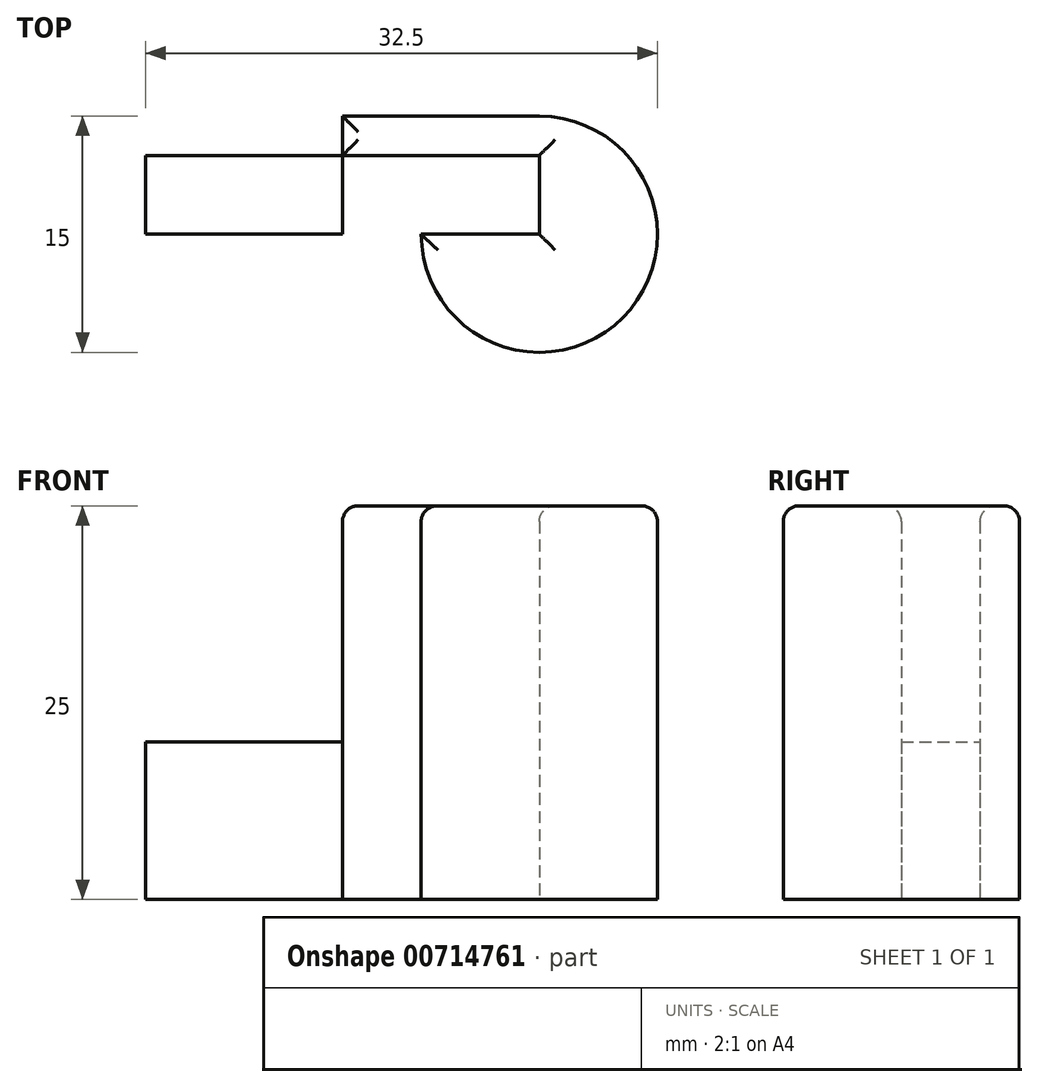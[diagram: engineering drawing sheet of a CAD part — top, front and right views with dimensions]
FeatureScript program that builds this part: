
annotation { "Feature Type Name" : "Feature", "Feature Type Description" : "" }
export const myFeature = defineFeature(function(context is Context, id is Id, definition is map)
    precondition{}
    {
        {
            var Q0;
            Q0=qCreatedBy(makeId("Top.planeOp"),FACE);
            var sketch = newSketch(context, id + "F0", { "sketchPlane" : qUnion([Q0])});
            skArc(sketch, "E0", {"start": v(-12.5, 5) * mm, "mid": v(-16.04, -3.54) * mm, "end": v(-7.5, 0) * mm});
            skArc(sketch, "E1", {"start": v(-7.5, 0) * mm, "mid": v(5.3, -5.3) * mm, "end": v(0, 7.5) * mm});
            skLineSegment(sketch, "E2", {"start": v(-12.5, 0) * mm, "end": v(0, 0) * mm, "construction": true});
            skLineSegment(sketch, "E3.bottom", {"start": v(-12.5, 0) * mm, "end": v(0, 0) * mm});
            skLineSegment(sketch, "E3.top", {"start": v(-12.5, 7.5) * mm, "end": v(0, 7.5) * mm});
            skLineSegment(sketch, "E3.left", {"start": v(-12.5, 0) * mm, "end": v(-12.5, 7.5) * mm});
            skLineSegment(sketch, "E3.right", {"start": v(0, 0) * mm, "end": v(0, 7.5) * mm});
            skArc(sketch, "E4.MirrorCS", {"start": v(12.5, 5) * mm, "mid": v(16.04, -3.54) * mm, "end": v(7.5, 0) * mm});
            skLineSegment(sketch, "E5.MirrorCS", {"start": v(12.5, 0) * mm, "end": v(12.5, 7.5) * mm});
            skLineSegment(sketch, "E6.MirrorCS", {"start": v(12.5, 7.5) * mm, "end": v(0, 7.5) * mm});
            skLineSegment(sketch, "E7.bottom", {"start": v(0, 0) * mm, "end": v(-25, 0) * mm});
            skLineSegment(sketch, "E7.top", {"start": v(0, 5) * mm, "end": v(-25, 5) * mm});
            skLineSegment(sketch, "E7.left", {"start": v(0, 0) * mm, "end": v(0, 5) * mm});
            skLineSegment(sketch, "E7.right", {"start": v(-25, 0) * mm, "end": v(-25, 5) * mm});
            skSolve(sketch);
        }
        {
            var Q0;
            {var subQ4=sQuery(id+"F0.wireOp",EDGE,"E3.right");Q0=makeQuery(id+"F0.imprint","IMPRINT",FACE,{"disambiguationData":[TD([[makeQuery(id+"F0.imprint","IMPRINT",EDGE,{"derivedFrom":subQ4}),-1.0]])]});}
            var Q1;
            {var subQ5=sQuery(id+"F0.wireOp",EDGE,"E3.top");Q1=makeQuery(id+"F0.imprint","IMPRINT",FACE,{"disambiguationData":[TD([[makeQuery(id+"F0.imprint","IMPRINT",EDGE,{"derivedFrom":subQ5}),-1.0]])]});}
            extrude(context, id + "F1", {"entities" : qUnion([Q0, Q1]), "depth" : 25 * mm, "offsetDistance" : 25 * mm});
        }
        {
            var Q0;
            Q0=makeQuery(id+"F1.opExtrude","CAP_FACE",FACE,{"disambiguationData":[OSD([sQuery(id+"F0.wireOp",EDGE,"E1"),sQuery(id+"F0.wireOp",EDGE,"E3.bottom"),sQuery(id+"F0.wireOp",EDGE,"E3.top"),sQuery(id+"F0.wireOp",EDGE,"E3.left")])],"isStart":false});
            fillet(context, id + "F2", {"entities" : qUnion([Q0]), "radius" : 1 * mm, "tangentPropagation" : true, "allowEdgeOverflow" : false});
        }
        {
            var Q0;
            {var subQ5=sQuery(id+"F0.wireOp",EDGE,"E7.left");Q0=makeQuery(id+"F0.imprint","IMPRINT",FACE,{"disambiguationData":[TD([[makeQuery(id+"F0.imprint","IMPRINT",EDGE,{"derivedFrom":subQ5}),1.0]])]});}
            var Q1;
            {var subQ0=sQuery(id+"F0.wireOp",EDGE,"E3.left");var subQ3=sQuery(id+"F0.wireOp",EDGE,"E7.bottom");var subQ5=makeQuery(id+"F0.imprint","INTERSECT",VERTEX,{"derivedFrom":[subQ0,subQ3]});Q1=makeQuery(id+"F0.imprint","IMPRINT",FACE,{"disambiguationData":[TD([[makeQuery(id+"F0.imprint","IMPRINT",EDGE,{"disambiguationData":[TD([[subQ5,-1.0]])],"derivedFrom":subQ3}),-1.0]])]});}
            var Q2;
            {var subQ5=sQuery(id+"F0.wireOp",EDGE,"E7.right");Q2=makeQuery(id+"F0.imprint","IMPRINT",FACE,{"disambiguationData":[TD([[makeQuery(id+"F0.imprint","IMPRINT",EDGE,{"derivedFrom":subQ5}),-1.0]])]});}
            extrude(context, id + "F3", {"entities" : qUnion([Q0, Q1, Q2]), "operationType" : NewBodyOperationType.ADD, "depth" : 10 * mm, "offsetDistance" : 25 * mm});
        }
    });
